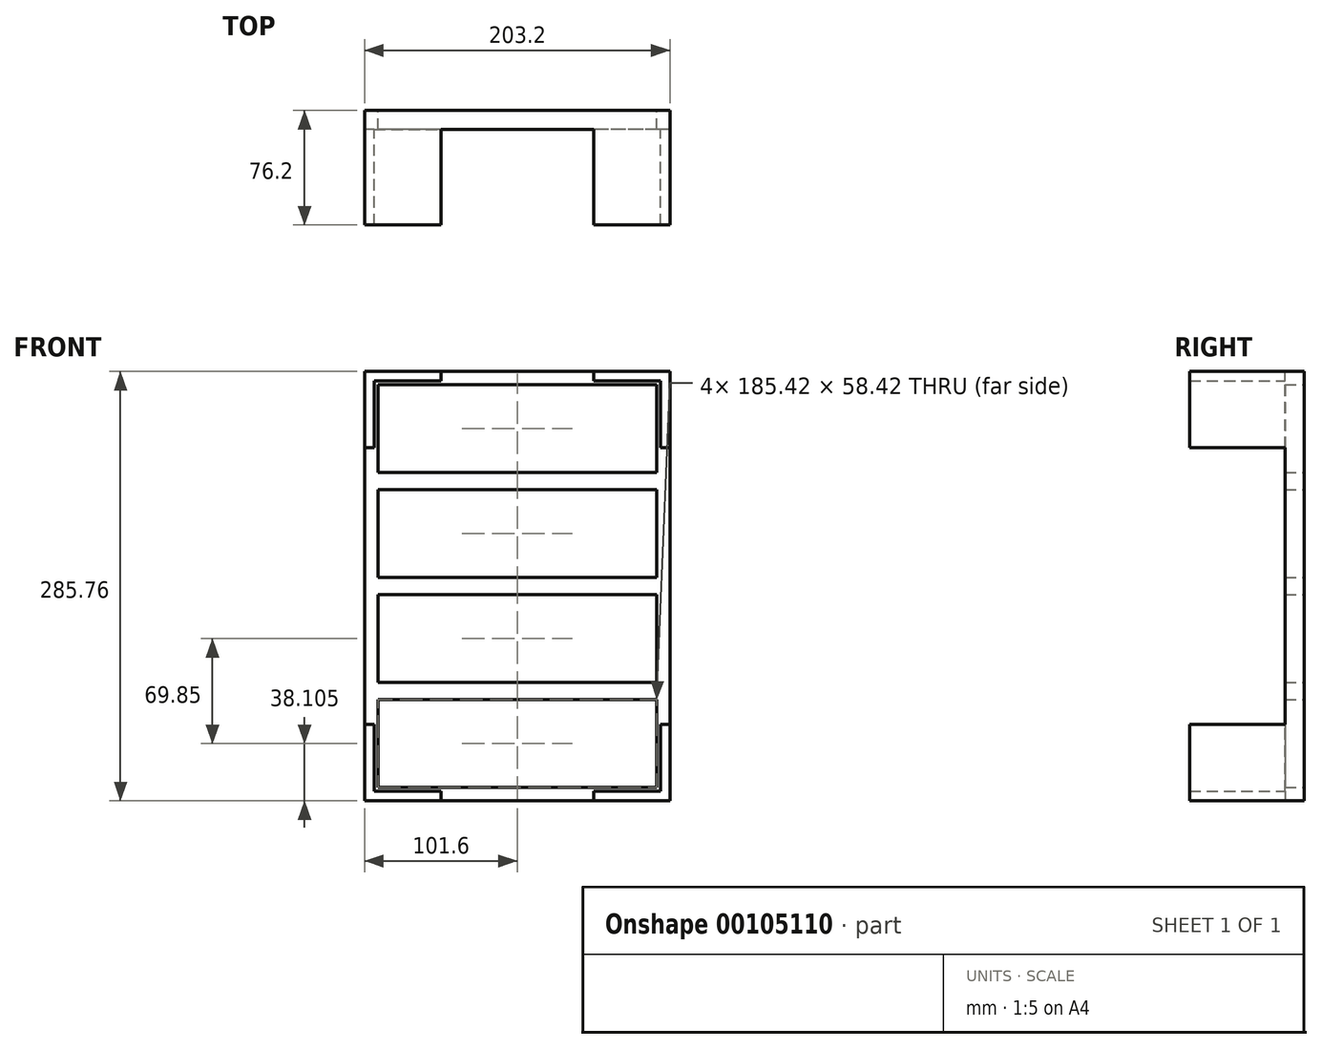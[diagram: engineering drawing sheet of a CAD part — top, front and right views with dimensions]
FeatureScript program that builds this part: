
annotation { "Feature Type Name" : "Feature", "Feature Type Description" : "" }
export const myFeature = defineFeature(function(context is Context, id is Id, definition is map)
    precondition{}
    {
        {
            var Q0;
            Q0=qCreatedBy(makeId("Front.planeOp"),FACE);
            var sketch = newSketch(context, id + "F0", { "sketchPlane" : qUnion([Q0])});
            skLineSegment(sketch, "E0.bottom", {"start": v(101.6, 142.88) * mm, "end": v(-101.6, 142.88) * mm});
            skLineSegment(sketch, "E0.top", {"start": v(101.6, -142.88) * mm, "end": v(-101.6, -142.88) * mm});
            skLineSegment(sketch, "E0.left", {"start": v(101.6, 142.88) * mm, "end": v(101.6, -142.88) * mm});
            skLineSegment(sketch, "E0.right", {"start": v(-101.6, 142.88) * mm, "end": v(-101.6, -142.88) * mm});
            skPoint(sketch, "E0.middle", {"position": v(0, 0) * mm});
            skLineSegment(sketch, "E1.bottom", {"start": v(-95.25, 73.02) * mm, "end": v(95.25, 73.03) * mm});
            skLineSegment(sketch, "E1.top", {"start": v(-95.25, 136.52) * mm, "end": v(95.25, 136.53) * mm});
            skLineSegment(sketch, "E1.left", {"start": v(-95.25, 73.02) * mm, "end": v(-95.25, 136.52) * mm});
            skLineSegment(sketch, "E1.right", {"start": v(95.25, 73.03) * mm, "end": v(95.25, 136.53) * mm});
            skLineSegment(sketch, "E2.bottom", {"start": v(-95.25, 3.17) * mm, "end": v(95.25, 3.18) * mm});
            skLineSegment(sketch, "E2.top", {"start": v(-95.25, 66.67) * mm, "end": v(95.25, 66.68) * mm});
            skLineSegment(sketch, "E2.left", {"start": v(-95.25, 3.17) * mm, "end": v(-95.25, 66.67) * mm});
            skLineSegment(sketch, "E2.right", {"start": v(95.25, 3.18) * mm, "end": v(95.25, 66.68) * mm});
            skLineSegment(sketch, "E3.bottom", {"start": v(-95.25, -66.68) * mm, "end": v(95.25, -66.67) * mm});
            skLineSegment(sketch, "E3.top", {"start": v(-95.25, -3.18) * mm, "end": v(95.25, -3.17) * mm});
            skLineSegment(sketch, "E3.left", {"start": v(-95.25, -66.68) * mm, "end": v(-95.25, -3.18) * mm});
            skLineSegment(sketch, "E3.right", {"start": v(95.25, -66.67) * mm, "end": v(95.25, -3.17) * mm});
            skLineSegment(sketch, "E4.bottom", {"start": v(-95.25, -136.53) * mm, "end": v(95.25, -136.52) * mm});
            skLineSegment(sketch, "E4.top", {"start": v(-95.25, -73.03) * mm, "end": v(95.25, -73.02) * mm});
            skLineSegment(sketch, "E4.left", {"start": v(-95.25, -136.53) * mm, "end": v(-95.25, -73.03) * mm});
            skLineSegment(sketch, "E4.right", {"start": v(95.25, -136.52) * mm, "end": v(95.25, -73.02) * mm});
            skLineSegment(sketch, "E5.bottom", {"start": v(92.71, 133.99) * mm, "end": v(-92.7, 133.98) * mm});
            skLineSegment(sketch, "E5.top", {"start": v(92.71, 75.57) * mm, "end": v(-92.7, 75.56) * mm});
            skLineSegment(sketch, "E5.left", {"start": v(92.71, 133.99) * mm, "end": v(92.71, 75.57) * mm});
            skLineSegment(sketch, "E5.right", {"start": v(-92.7, 133.98) * mm, "end": v(-92.7, 75.56) * mm});
            skLineSegment(sketch, "E6.bottom", {"start": v(92.7, 64.14) * mm, "end": v(-92.7, 64.13) * mm});
            skLineSegment(sketch, "E6.top", {"start": v(92.7, 5.72) * mm, "end": v(-92.7, 5.71) * mm});
            skLineSegment(sketch, "E6.left", {"start": v(92.7, 64.14) * mm, "end": v(92.7, 5.72) * mm});
            skLineSegment(sketch, "E6.right", {"start": v(-92.7, 64.13) * mm, "end": v(-92.7, 5.71) * mm});
            skLineSegment(sketch, "E7.bottom", {"start": v(92.7, -5.71) * mm, "end": v(-92.7, -5.72) * mm});
            skLineSegment(sketch, "E7.top", {"start": v(92.7, -64.13) * mm, "end": v(-92.7, -64.13) * mm});
            skLineSegment(sketch, "E7.left", {"start": v(92.7, -5.71) * mm, "end": v(92.7, -64.13) * mm});
            skLineSegment(sketch, "E7.right", {"start": v(-92.7, -5.72) * mm, "end": v(-92.7, -64.13) * mm});
            skLineSegment(sketch, "E8.bottom", {"start": v(92.7, -75.56) * mm, "end": v(-92.71, -75.57) * mm});
            skLineSegment(sketch, "E8.top", {"start": v(92.7, -133.98) * mm, "end": v(-92.7, -133.98) * mm});
            skLineSegment(sketch, "E8.left", {"start": v(92.7, -75.56) * mm, "end": v(92.7, -133.98) * mm});
            skLineSegment(sketch, "E8.right", {"start": v(-92.71, -75.57) * mm, "end": v(-92.7, -133.98) * mm});
            skSolve(sketch);
        }
        {
            var Q0;
            Q0=makeQuery(id+"F0.imprint","IMPRINT",FACE,{"disambiguationData":[TD([[makeQuery(id+"F0.imprint","IMPRINT",EDGE,{"derivedFrom":sQuery(id+"F0.wireOp",EDGE,"E0.bottom")}),1.0]])]});
            var Q1;
            Q1=makeQuery(id+"F0.imprint","IMPRINT",FACE,{"disambiguationData":[TD([[makeQuery(id+"F0.imprint","IMPRINT",EDGE,{"derivedFrom":sQuery(id+"F0.wireOp",EDGE,"E1.bottom")}),1.0]])]});
            var Q2;
            Q2=makeQuery(id+"F0.imprint","IMPRINT",FACE,{"disambiguationData":[TD([[makeQuery(id+"F0.imprint","IMPRINT",EDGE,{"derivedFrom":sQuery(id+"F0.wireOp",EDGE,"E2.bottom")}),1.0]])]});
            var Q3;
            Q3=makeQuery(id+"F0.imprint","IMPRINT",FACE,{"disambiguationData":[TD([[makeQuery(id+"F0.imprint","IMPRINT",EDGE,{"derivedFrom":sQuery(id+"F0.wireOp",EDGE,"E3.bottom")}),1.0]])]});
            var Q4;
            Q4=makeQuery(id+"F0.imprint","IMPRINT",FACE,{"disambiguationData":[TD([[makeQuery(id+"F0.imprint","IMPRINT",EDGE,{"derivedFrom":sQuery(id+"F0.wireOp",EDGE,"E4.bottom")}),1.0]])]});
            extrude(context, id + "F1", {"entities" : qUnion([Q0, Q1, Q2, Q3, Q4]), "depth" : 12.7 * mm});
        }
        {
            var Q0;
            Q0=sQuery(id+"F0.wireOp",EDGE,"E1.bottom");
            var Q1;
            Q1=sQuery(id+"F0.wireOp",EDGE,"E1.left");
            var Q2;
            Q2=sQuery(id+"F0.wireOp",EDGE,"E1.top");
            var Q3;
            Q3=sQuery(id+"F0.wireOp",EDGE,"E1.right");
            var Q4;
            Q4=sQuery(id+"F0.wireOp",EDGE,"E2.right");
            var Q5;
            Q5=sQuery(id+"F0.wireOp",EDGE,"E2.left");
            var Q6;
            Q6=sQuery(id+"F0.wireOp",EDGE,"E2.top");
            var Q7;
            Q7=sQuery(id+"F0.wireOp",EDGE,"E2.bottom");
            var Q8;
            Q8=sQuery(id+"F0.wireOp",EDGE,"E3.top");
            var Q9;
            Q9=sQuery(id+"F0.wireOp",EDGE,"E3.left");
            var Q10;
            Q10=sQuery(id+"F0.wireOp",EDGE,"E3.bottom");
            var Q11;
            Q11=sQuery(id+"F0.wireOp",EDGE,"E4.top");
            var Q12;
            Q12=sQuery(id+"F0.wireOp",EDGE,"E3.right");
            var Q13;
            Q13=sQuery(id+"F0.wireOp",EDGE,"E4.right");
            var Q14;
            Q14=sQuery(id+"F0.wireOp",EDGE,"E4.bottom");
            var Q15;
            Q15=sQuery(id+"F0.wireOp",EDGE,"E4.left");
            extrude(context, id + "F2", {"bodyType" : ToolBodyType.SURFACE, "surfaceEntities" : qUnion([Q0, Q1, Q2, Q3, Q4, Q5, Q6, Q7, Q8, Q9, Q10, Q11, Q12, Q13, Q14, Q15]), "oppositeDirection" : true, "depth" : 2.54 * mm});
        }
        {
            var Q0;
            Q0=makeQuery(id+"F1.opExtrude","CAP_FACE",FACE,{"disambiguationData":[OSD([sQuery(id+"F0.wireOp",EDGE,"E0.bottom"),sQuery(id+"F0.wireOp",EDGE,"E0.top"),sQuery(id+"F0.wireOp",EDGE,"E0.left"),sQuery(id+"F0.wireOp",EDGE,"E0.right")])],"isStart":false});
            var sketch = newSketch(context, id + "F3", { "sketchPlane" : qUnion([Q0])});
            skLineSegment(sketch, "E9.bottom", {"start": v(101.6, -142.88) * mm, "end": v(95.25, -142.88) * mm});
            skLineSegment(sketch, "E9.top", {"start": v(101.6, -92.07) * mm, "end": v(95.25, -92.07) * mm});
            skLineSegment(sketch, "E9.left", {"start": v(101.6, -142.88) * mm, "end": v(101.6, -92.07) * mm});
            skLineSegment(sketch, "E9.right", {"start": v(95.25, -142.88) * mm, "end": v(95.25, -92.07) * mm});
            skLineSegment(sketch, "E10.bottom", {"start": v(101.6, -142.88) * mm, "end": v(50.8, -142.88) * mm});
            skLineSegment(sketch, "E10.top", {"start": v(101.6, -136.53) * mm, "end": v(50.8, -136.53) * mm});
            skLineSegment(sketch, "E10.left", {"start": v(101.6, -142.88) * mm, "end": v(101.6, -136.53) * mm});
            skLineSegment(sketch, "E10.right", {"start": v(50.8, -142.88) * mm, "end": v(50.8, -136.53) * mm});
            skLineSegment(sketch, "E11.bottom", {"start": v(101.6, 92.07) * mm, "end": v(95.25, 92.07) * mm});
            skLineSegment(sketch, "E11.top", {"start": v(101.6, 142.88) * mm, "end": v(95.25, 142.88) * mm});
            skLineSegment(sketch, "E11.left", {"start": v(101.6, 92.07) * mm, "end": v(101.6, 142.88) * mm});
            skLineSegment(sketch, "E11.right", {"start": v(95.25, 92.07) * mm, "end": v(95.25, 142.88) * mm});
            skLineSegment(sketch, "E12.bottom", {"start": v(-95.25, -142.88) * mm, "end": v(-101.6, -142.88) * mm});
            skLineSegment(sketch, "E12.top", {"start": v(-95.25, -92.08) * mm, "end": v(-101.6, -92.08) * mm});
            skLineSegment(sketch, "E12.left", {"start": v(-95.25, -142.88) * mm, "end": v(-95.25, -92.08) * mm});
            skLineSegment(sketch, "E12.right", {"start": v(-101.6, -142.88) * mm, "end": v(-101.6, -92.08) * mm});
            skLineSegment(sketch, "E13.bottom", {"start": v(-95.25, 92.07) * mm, "end": v(-101.6, 92.07) * mm});
            skLineSegment(sketch, "E13.top", {"start": v(-95.25, 142.88) * mm, "end": v(-101.6, 142.88) * mm});
            skLineSegment(sketch, "E13.left", {"start": v(-95.25, 92.07) * mm, "end": v(-95.25, 142.88) * mm});
            skLineSegment(sketch, "E13.right", {"start": v(-101.6, 92.07) * mm, "end": v(-101.6, 142.88) * mm});
            skLineSegment(sketch, "E14.bottom", {"start": v(-50.8, 136.53) * mm, "end": v(-101.6, 136.53) * mm});
            skLineSegment(sketch, "E14.top", {"start": v(-50.8, 142.88) * mm, "end": v(-101.6, 142.88) * mm});
            skLineSegment(sketch, "E14.left", {"start": v(-50.8, 136.53) * mm, "end": v(-50.8, 142.88) * mm});
            skLineSegment(sketch, "E14.right", {"start": v(-101.6, 136.53) * mm, "end": v(-101.6, 142.88) * mm});
            skLineSegment(sketch, "E15.bottom", {"start": v(101.6, 136.52) * mm, "end": v(50.8, 136.52) * mm});
            skLineSegment(sketch, "E15.top", {"start": v(101.6, 142.87) * mm, "end": v(50.8, 142.87) * mm});
            skLineSegment(sketch, "E15.left", {"start": v(101.6, 136.52) * mm, "end": v(101.6, 142.88) * mm});
            skLineSegment(sketch, "E15.right", {"start": v(50.8, 136.52) * mm, "end": v(50.8, 142.87) * mm});
            skLineSegment(sketch, "E16.bottom", {"start": v(-101.6, -136.53) * mm, "end": v(-50.8, -136.53) * mm});
            skLineSegment(sketch, "E16.top", {"start": v(-101.6, -142.88) * mm, "end": v(-50.8, -142.88) * mm});
            skLineSegment(sketch, "E16.left", {"start": v(-101.6, -136.53) * mm, "end": v(-101.6, -142.88) * mm});
            skLineSegment(sketch, "E16.right", {"start": v(-50.8, -136.53) * mm, "end": v(-50.8, -142.88) * mm});
            skSolve(sketch);
        }
        {
            var Q0;
            Q0 = qSketchRegion(id + "F3", true);
            extrude(context, id + "F4", {"entities" : qUnion([Q0]), "operationType" : NewBodyOperationType.ADD, "depth" : 63.5 * mm});
        }
    });
